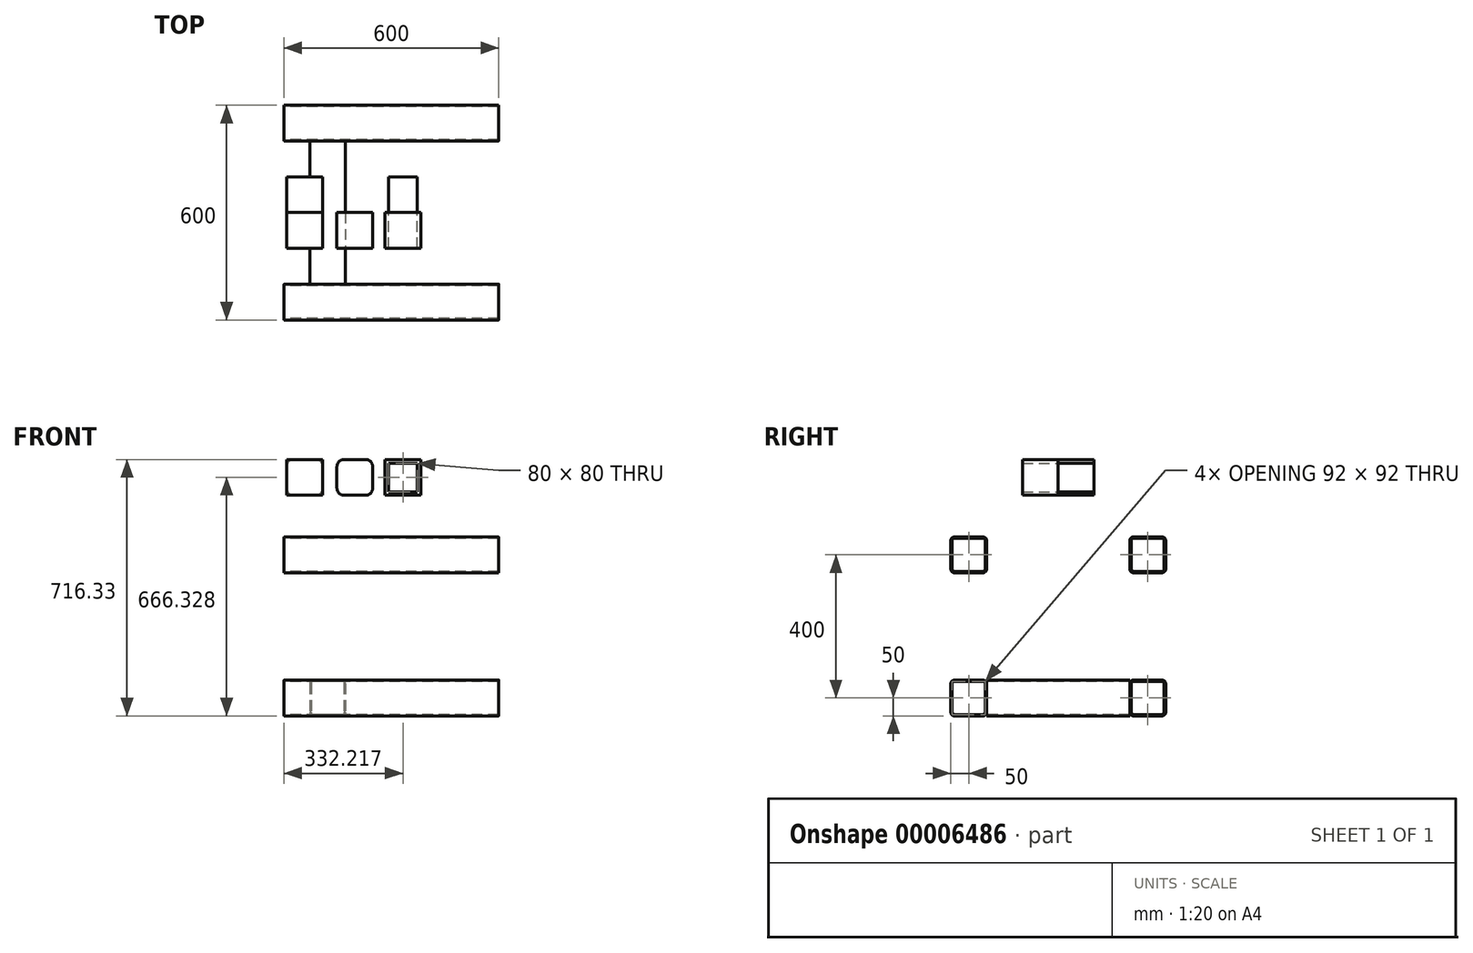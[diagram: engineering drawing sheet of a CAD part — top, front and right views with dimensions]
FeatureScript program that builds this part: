
annotation { "Feature Type Name" : "Feature", "Feature Type Description" : "" }
export const myFeature = defineFeature(function(context is Context, id is Id, definition is map)
    precondition{}
    {
        {
            var Q0;
            Q0=qCreatedBy(makeId("Right.planeOp"),FACE);
            var sketch = newSketch(context, id + "F0", { "sketchPlane" : qUnion([Q0])});
            skLineSegment(sketch, "E0.rect.bottom", {"start": v(-210, 0) * mm, "end": v(-290, 0) * mm});
            skLineSegment(sketch, "E0.rect.top", {"start": v(-210, -100) * mm, "end": v(-290, -100) * mm});
            skLineSegment(sketch, "E0.rect.left", {"start": v(-200, -10) * mm, "end": v(-200, -90) * mm});
            skLineSegment(sketch, "E0.rect.right", {"start": v(-300, -10) * mm, "end": v(-300, -90) * mm});
            skPoint(sketch, "E0.rect.middle", {"position": v(-250, -50) * mm});
            skPoint(sketch, "E1.visualSharp", {"position": v(-300, 0) * mm});
            skArc(sketch, "E1.filletArc", {"start": v(-290, 0) * mm, "mid": v(-297.07, -2.93) * mm, "end": v(-300, -10) * mm});
            skPoint(sketch, "E2.visualSharp", {"position": v(-200, 0) * mm});
            skArc(sketch, "E2.filletArc", {"start": v(-200, -10) * mm, "mid": v(-202.93, -2.93) * mm, "end": v(-210, 0) * mm});
            skPoint(sketch, "E3.visualSharp", {"position": v(-200, -100) * mm});
            skArc(sketch, "E3.filletArc", {"start": v(-210, -100) * mm, "mid": v(-202.93, -97.07) * mm, "end": v(-200, -90) * mm});
            skPoint(sketch, "E4.visualSharp", {"position": v(-300, -100) * mm});
            skArc(sketch, "E4.filletArc", {"start": v(-300, -90) * mm, "mid": v(-297.07, -97.07) * mm, "end": v(-290, -100) * mm});
            skArc(sketch, "E5.0", {"start": v(-204, -10) * mm, "mid": v(-205.76, -5.76) * mm, "end": v(-210, -4) * mm});
            skLineSegment(sketch, "E5.1", {"start": v(-204, -10) * mm, "end": v(-204, -90) * mm});
            skArc(sketch, "E5.2", {"start": v(-210, -96) * mm, "mid": v(-205.76, -94.24) * mm, "end": v(-204, -90) * mm});
            skLineSegment(sketch, "E5.3", {"start": v(-210, -96) * mm, "end": v(-290, -96) * mm});
            skArc(sketch, "E5.4", {"start": v(-296, -90) * mm, "mid": v(-294.24, -94.24) * mm, "end": v(-290, -96) * mm});
            skLineSegment(sketch, "E5.5", {"start": v(-210, -4) * mm, "end": v(-290, -4) * mm});
            skLineSegment(sketch, "E5.6", {"start": v(-296, -10) * mm, "end": v(-296, -90) * mm});
            skArc(sketch, "E5.7", {"start": v(-290, -4) * mm, "mid": v(-294.24, -5.76) * mm, "end": v(-296, -10) * mm});
            skLineSegment(sketch, "E6.0.1.0", {"start": v(-200, -410) * mm, "end": v(-200, -490) * mm});
            skPoint(sketch, "E6.0.1.1", {"position": v(-300, -400) * mm});
            skLineSegment(sketch, "E6.0.1.2", {"start": v(-210, -500) * mm, "end": v(-290, -500) * mm});
            skArc(sketch, "E6.0.1.3", {"start": v(-290, -400) * mm, "mid": v(-297.07, -402.93) * mm, "end": v(-300, -410) * mm});
            skPoint(sketch, "E6.0.1.4", {"position": v(-200, -500) * mm});
            skLineSegment(sketch, "E6.0.1.5", {"start": v(-210, -400) * mm, "end": v(-290, -400) * mm});
            skPoint(sketch, "E6.0.1.6", {"position": v(-300, -500) * mm});
            skLineSegment(sketch, "E6.0.1.7", {"start": v(-210, -496) * mm, "end": v(-290, -496) * mm});
            skLineSegment(sketch, "E6.0.1.8", {"start": v(-296, -410) * mm, "end": v(-296, -490) * mm});
            skPoint(sketch, "E6.0.1.9", {"position": v(-200, -400) * mm});
            skLineSegment(sketch, "E6.0.1.10", {"start": v(-204, -410) * mm, "end": v(-204, -490) * mm});
            skArc(sketch, "E6.0.1.11", {"start": v(-300, -490) * mm, "mid": v(-297.07, -497.07) * mm, "end": v(-290, -500) * mm});
            skArc(sketch, "E6.0.1.12", {"start": v(-204, -410) * mm, "mid": v(-205.76, -405.76) * mm, "end": v(-210, -404) * mm});
            skArc(sketch, "E6.0.1.13", {"start": v(-210, -500) * mm, "mid": v(-202.93, -497.07) * mm, "end": v(-200, -490) * mm});
            skLineSegment(sketch, "E6.0.1.14", {"start": v(-210, -404) * mm, "end": v(-290, -404) * mm});
            skLineSegment(sketch, "E6.0.1.15", {"start": v(-300, -410) * mm, "end": v(-300, -490) * mm});
            skArc(sketch, "E6.0.1.16", {"start": v(-296, -490) * mm, "mid": v(-294.24, -494.24) * mm, "end": v(-290, -496) * mm});
            skArc(sketch, "E6.0.1.17", {"start": v(-290, -404) * mm, "mid": v(-294.24, -405.76) * mm, "end": v(-296, -410) * mm});
            skArc(sketch, "E6.0.1.18", {"start": v(-210, -496) * mm, "mid": v(-205.76, -494.24) * mm, "end": v(-204, -490) * mm});
            skArc(sketch, "E6.0.1.19", {"start": v(-200, -410) * mm, "mid": v(-202.93, -402.93) * mm, "end": v(-210, -400) * mm});
            skPoint(sketch, "E6.0.1.20", {"position": v(-250, -450) * mm});
            skLineSegment(sketch, "E6.1.0.0", {"start": v(300, -10) * mm, "end": v(300, -90) * mm});
            skPoint(sketch, "E6.1.0.1", {"position": v(200, 0) * mm});
            skLineSegment(sketch, "E6.1.0.2", {"start": v(290, -100) * mm, "end": v(210, -100) * mm});
            skArc(sketch, "E6.1.0.3", {"start": v(210, 0) * mm, "mid": v(202.93, -2.93) * mm, "end": v(200, -10) * mm});
            skPoint(sketch, "E6.1.0.4", {"position": v(300, -100) * mm});
            skLineSegment(sketch, "E6.1.0.5", {"start": v(290, 0) * mm, "end": v(210, 0) * mm});
            skPoint(sketch, "E6.1.0.6", {"position": v(200, -100) * mm});
            skLineSegment(sketch, "E6.1.0.7", {"start": v(290, -96) * mm, "end": v(210, -96) * mm});
            skLineSegment(sketch, "E6.1.0.8", {"start": v(204, -10) * mm, "end": v(204, -90) * mm});
            skPoint(sketch, "E6.1.0.9", {"position": v(300, 0) * mm});
            skLineSegment(sketch, "E6.1.0.10", {"start": v(296, -10) * mm, "end": v(296, -90) * mm});
            skArc(sketch, "E6.1.0.11", {"start": v(200, -90) * mm, "mid": v(202.93, -97.07) * mm, "end": v(210, -100) * mm});
            skArc(sketch, "E6.1.0.12", {"start": v(296, -10) * mm, "mid": v(294.24, -5.76) * mm, "end": v(290, -4) * mm});
            skArc(sketch, "E6.1.0.13", {"start": v(290, -100) * mm, "mid": v(297.07, -97.07) * mm, "end": v(300, -90) * mm});
            skLineSegment(sketch, "E6.1.0.14", {"start": v(290, -4) * mm, "end": v(210, -4) * mm});
            skLineSegment(sketch, "E6.1.0.15", {"start": v(200, -10) * mm, "end": v(200, -90) * mm});
            skArc(sketch, "E6.1.0.16", {"start": v(204, -90) * mm, "mid": v(205.76, -94.24) * mm, "end": v(210, -96) * mm});
            skArc(sketch, "E6.1.0.17", {"start": v(210, -4) * mm, "mid": v(205.76, -5.76) * mm, "end": v(204, -10) * mm});
            skArc(sketch, "E6.1.0.18", {"start": v(290, -96) * mm, "mid": v(294.24, -94.24) * mm, "end": v(296, -90) * mm});
            skArc(sketch, "E6.1.0.19", {"start": v(300, -10) * mm, "mid": v(297.07, -2.93) * mm, "end": v(290, 0) * mm});
            skPoint(sketch, "E6.1.0.20", {"position": v(250, -50) * mm});
            skLineSegment(sketch, "E6.1.1.0", {"start": v(300, -410) * mm, "end": v(300, -490) * mm});
            skPoint(sketch, "E6.1.1.1", {"position": v(200, -400) * mm});
            skLineSegment(sketch, "E6.1.1.2", {"start": v(290, -500) * mm, "end": v(210, -500) * mm});
            skArc(sketch, "E6.1.1.3", {"start": v(210, -400) * mm, "mid": v(202.93, -402.93) * mm, "end": v(200, -410) * mm});
            skPoint(sketch, "E6.1.1.4", {"position": v(300, -500) * mm});
            skLineSegment(sketch, "E6.1.1.5", {"start": v(290, -400) * mm, "end": v(210, -400) * mm});
            skPoint(sketch, "E6.1.1.6", {"position": v(200, -500) * mm});
            skLineSegment(sketch, "E6.1.1.7", {"start": v(290, -496) * mm, "end": v(210, -496) * mm});
            skLineSegment(sketch, "E6.1.1.8", {"start": v(204, -410) * mm, "end": v(204, -490) * mm});
            skPoint(sketch, "E6.1.1.9", {"position": v(300, -400) * mm});
            skLineSegment(sketch, "E6.1.1.10", {"start": v(296, -410) * mm, "end": v(296, -490) * mm});
            skArc(sketch, "E6.1.1.11", {"start": v(200, -490) * mm, "mid": v(202.93, -497.07) * mm, "end": v(210, -500) * mm});
            skArc(sketch, "E6.1.1.12", {"start": v(296, -410) * mm, "mid": v(294.24, -405.76) * mm, "end": v(290, -404) * mm});
            skArc(sketch, "E6.1.1.13", {"start": v(290, -500) * mm, "mid": v(297.07, -497.07) * mm, "end": v(300, -490) * mm});
            skLineSegment(sketch, "E6.1.1.14", {"start": v(290, -404) * mm, "end": v(210, -404) * mm});
            skLineSegment(sketch, "E6.1.1.15", {"start": v(200, -410) * mm, "end": v(200, -490) * mm});
            skArc(sketch, "E6.1.1.16", {"start": v(204, -490) * mm, "mid": v(205.76, -494.24) * mm, "end": v(210, -496) * mm});
            skArc(sketch, "E6.1.1.17", {"start": v(210, -404) * mm, "mid": v(205.76, -405.76) * mm, "end": v(204, -410) * mm});
            skArc(sketch, "E6.1.1.18", {"start": v(290, -496) * mm, "mid": v(294.24, -494.24) * mm, "end": v(296, -490) * mm});
            skArc(sketch, "E6.1.1.19", {"start": v(300, -410) * mm, "mid": v(297.07, -402.93) * mm, "end": v(290, -400) * mm});
            skPoint(sketch, "E6.1.1.20", {"position": v(250, -450) * mm});
            skLineSegment(sketch, "E6.direction1", {"start": v(-250, -50) * mm, "end": v(250, -50) * mm, "construction": true});
            skLineSegment(sketch, "E6.direction2", {"start": v(-250, -50) * mm, "end": v(-250, -450) * mm, "construction": true});
            skLineSegment(sketch, "E7", {"start": v(0, 0) * mm, "end": v(0, -50) * mm, "construction": true});
            skSolve(sketch);
        }
        {
            var Q0;
            Q0=makeQuery(id+"F0.imprint","IMPRINT",FACE,{"disambiguationData":[TD([[makeQuery(id+"F0.imprint","IMPRINT",EDGE,{"derivedFrom":sQuery(id+"F0.wireOp",EDGE,"E0.rect.bottom")}),1.0]])]});
            var Q1;
            Q1=makeQuery(id+"F0.imprint","IMPRINT",FACE,{"disambiguationData":[TD([[makeQuery(id+"F0.imprint","IMPRINT",EDGE,{"derivedFrom":sQuery(id+"F0.wireOp",EDGE,"E6.1.0.0")}),-1.0]])]});
            var Q2;
            Q2=makeQuery(id+"F0.imprint","IMPRINT",FACE,{"disambiguationData":[TD([[makeQuery(id+"F0.imprint","IMPRINT",EDGE,{"derivedFrom":sQuery(id+"F0.wireOp",EDGE,"E6.0.1.0")}),-1.0]])]});
            var Q3;
            Q3=makeQuery(id+"F0.imprint","IMPRINT",FACE,{"disambiguationData":[TD([[makeQuery(id+"F0.imprint","IMPRINT",EDGE,{"derivedFrom":sQuery(id+"F0.wireOp",EDGE,"E6.1.1.0")}),-1.0]])]});
            extrude(context, id + "F1", {"entities" : qUnion([Q0, Q1, Q2, Q3]), "endBound" : BoundingType.SYMMETRIC, "depth" : 600 * mm});
        }
        {
            var Q0;
            Q0=qCreatedBy(makeId("Front.planeOp"),FACE);
            var sketch = newSketch(context, id + "F2", { "sketchPlane" : qUnion([Q0])});
            skLineSegment(sketch, "E8.rect.bottom", {"start": v(-127.9, -400) * mm, "end": v(-227.9, -400) * mm});
            skLineSegment(sketch, "E8.rect.top", {"start": v(-127.9, -500) * mm, "end": v(-227.9, -500) * mm});
            skLineSegment(sketch, "E8.rect.left", {"start": v(-127.9, -400) * mm, "end": v(-127.9, -500) * mm});
            skLineSegment(sketch, "E8.rect.right", {"start": v(-227.9, -400) * mm, "end": v(-227.9, -500) * mm});
            skPoint(sketch, "E8.rect.middle", {"position": v(-177.9, -450) * mm});
            skLineSegment(sketch, "E9.0", {"start": v(300, -500) * mm, "end": v(-300, -500) * mm});
            skLineSegment(sketch, "E10.0", {"start": v(300, -400) * mm, "end": v(-300, -400) * mm});
            skLineSegment(sketch, "E11.0", {"start": v(-223.9, -404) * mm, "end": v(-223.9, -496) * mm});
            skLineSegment(sketch, "E11.1", {"start": v(-131.9, -404) * mm, "end": v(-223.9, -404) * mm});
            skLineSegment(sketch, "E11.2", {"start": v(-131.9, -404) * mm, "end": v(-131.9, -496) * mm});
            skLineSegment(sketch, "E11.3", {"start": v(-131.9, -496) * mm, "end": v(-223.9, -496) * mm});
            skSolve(sketch);
        }
        {
            var Q0;
            Q0=makeQuery(id+"F2.imprint","IMPRINT",FACE,{"disambiguationData":[TD([[makeQuery(id+"F2.imprint","IMPRINT",EDGE,{"derivedFrom":sQuery(id+"F2.wireOp",EDGE,"E8.rect.bottom")}),1.0]])]});
            var Q1;
            Q1=makeQuery(id+"F1.opExtrude","SWEPT_BODY",BODY,{"disambiguationData":[OSD([sQuery(id+"F0.wireOp",EDGE,"E6.1.1.0"),sQuery(id+"F0.wireOp",EDGE,"E6.1.1.2"),sQuery(id+"F0.wireOp",EDGE,"E6.1.1.3"),sQuery(id+"F0.wireOp",EDGE,"E6.1.1.5"),sQuery(id+"F0.wireOp",EDGE,"E6.1.1.7"),sQuery(id+"F0.wireOp",EDGE,"E6.1.1.8"),sQuery(id+"F0.wireOp",EDGE,"E6.1.1.10"),sQuery(id+"F0.wireOp",EDGE,"E6.1.1.11"),sQuery(id+"F0.wireOp",EDGE,"E6.1.1.12"),sQuery(id+"F0.wireOp",EDGE,"E6.1.1.13"),sQuery(id+"F0.wireOp",EDGE,"E6.1.1.14"),sQuery(id+"F0.wireOp",EDGE,"E6.1.1.15"),sQuery(id+"F0.wireOp",EDGE,"E6.1.1.16"),sQuery(id+"F0.wireOp",EDGE,"E6.1.1.17"),sQuery(id+"F0.wireOp",EDGE,"E6.1.1.18"),sQuery(id+"F0.wireOp",EDGE,"E6.1.1.19")])]});
            extrude(context, id + "F3", {"entities" : qUnion([Q0]), "operationType" : NewBodyOperationType.ADD, "endBound" : BoundingType.SYMMETRIC, "oppositeDirection" : true, "endBoundEntity" : qUnion([Q1]), "depth" : 400 * mm});
        }
        {
            var Q0;
            Q0=makeQuery(id+"F3.opExtrude","SWEPT_EDGE",EDGE,{"disambiguationData":[OSD([sQuery(id+"F2.wireOp",EDGE,"E8.rect.bottom"),sQuery(id+"F2.wireOp",EDGE,"E8.rect.left")])]});
            fillet(context, id + "F4", {"entities" : qUnion([Q0]), "radius" : 10 * mm, "tangentPropagation" : true, "allowEdgeOverflow" : false});
        }
        {
            var Q0;
            Q0=qCreatedBy(makeId("Front.planeOp"),FACE);
            var sketch = newSketch(context, id + "F5", { "sketchPlane" : qUnion([Q0])});
            skLineSegment(sketch, "E12.rect.bottom", {"start": v(-191.9, 116.33) * mm, "end": v(-291.9, 116.33) * mm});
            skLineSegment(sketch, "E12.rect.top", {"start": v(-191.9, 216.33) * mm, "end": v(-291.9, 216.33) * mm});
            skLineSegment(sketch, "E12.rect.left", {"start": v(-191.9, 116.33) * mm, "end": v(-191.9, 216.33) * mm});
            skLineSegment(sketch, "E12.rect.right", {"start": v(-291.9, 116.33) * mm, "end": v(-291.9, 216.33) * mm});
            skPoint(sketch, "E12.rect.middle", {"position": v(-241.9, 166.33) * mm});
            skLineSegment(sketch, "E13.rect.bottom", {"start": v(82.22, 216.33) * mm, "end": v(-17.78, 216.33) * mm});
            skLineSegment(sketch, "E13.rect.top", {"start": v(82.22, 116.33) * mm, "end": v(-17.78, 116.33) * mm});
            skLineSegment(sketch, "E13.rect.left", {"start": v(82.22, 216.33) * mm, "end": v(82.22, 116.33) * mm});
            skLineSegment(sketch, "E13.rect.right", {"start": v(-17.78, 216.33) * mm, "end": v(-17.78, 116.33) * mm});
            skPoint(sketch, "E13.rect.middle", {"position": v(32.22, 166.33) * mm});
            skLineSegment(sketch, "E14.rect.bottom", {"start": v(-72.15, 216.33) * mm, "end": v(-132.15, 216.33) * mm});
            skLineSegment(sketch, "E14.rect.top", {"start": v(-72.15, 116.33) * mm, "end": v(-132.15, 116.33) * mm});
            skLineSegment(sketch, "E14.rect.left", {"start": v(-52.15, 196.33) * mm, "end": v(-52.15, 136.33) * mm});
            skLineSegment(sketch, "E14.rect.right", {"start": v(-152.15, 196.33) * mm, "end": v(-152.15, 136.33) * mm});
            skPoint(sketch, "E14.rect.middle", {"position": v(-102.15, 166.33) * mm});
            skPoint(sketch, "E15.visualSharp", {"position": v(-152.15, 216.33) * mm});
            skArc(sketch, "E15.filletArc", {"start": v(-132.15, 216.33) * mm, "mid": v(-146.29, 210.47) * mm, "end": v(-152.15, 196.33) * mm});
            skPoint(sketch, "E16.visualSharp", {"position": v(-52.15, 216.33) * mm});
            skArc(sketch, "E16.filletArc", {"start": v(-52.15, 196.33) * mm, "mid": v(-58, 210.47) * mm, "end": v(-72.15, 216.33) * mm});
            skPoint(sketch, "E17.visualSharp", {"position": v(-52.15, 116.33) * mm});
            skArc(sketch, "E17.filletArc", {"start": v(-72.15, 116.33) * mm, "mid": v(-58, 122.19) * mm, "end": v(-52.15, 136.33) * mm});
            skPoint(sketch, "E18.visualSharp", {"position": v(-152.15, 116.33) * mm});
            skArc(sketch, "E18.filletArc", {"start": v(-152.15, 136.33) * mm, "mid": v(-146.29, 122.19) * mm, "end": v(-132.15, 116.33) * mm});
            skLineSegment(sketch, "E19.0", {"start": v(72.22, 206.33) * mm, "end": v(-7.78, 206.33) * mm});
            skLineSegment(sketch, "E19.1", {"start": v(72.22, 206.33) * mm, "end": v(72.22, 126.33) * mm});
            skLineSegment(sketch, "E19.2", {"start": v(72.22, 126.33) * mm, "end": v(-7.78, 126.33) * mm});
            skLineSegment(sketch, "E19.3", {"start": v(-7.78, 206.33) * mm, "end": v(-7.78, 126.33) * mm});
            skSolve(sketch);
        }
        {
            var Q0;
            Q0=makeQuery(id+"F5.imprint","IMPRINT",FACE,{"disambiguationData":[TD([[makeQuery(id+"F5.imprint","IMPRINT",EDGE,{"derivedFrom":sQuery(id+"F5.wireOp",EDGE,"E12.rect.bottom")}),-1.0]])]});
            extrude(context, id + "F6", {"entities" : qUnion([Q0]), "depth" : 100 * mm});
        }
        {
            var Q0;
            Q0=makeQuery(id+"F5.imprint","IMPRINT",FACE,{"disambiguationData":[TD([[makeQuery(id+"F5.imprint","IMPRINT",EDGE,{"derivedFrom":sQuery(id+"F5.wireOp",EDGE,"E14.rect.bottom")}),1.0]])]});
            extrude(context, id + "F7", {"entities" : qUnion([Q0]), "depth" : 100 * mm});
        }
        {
            var Q0;
            Q0=makeQuery(id+"F5.imprint","IMPRINT",FACE,{"disambiguationData":[TD([[makeQuery(id+"F5.imprint","IMPRINT",EDGE,{"derivedFrom":sQuery(id+"F5.wireOp",EDGE,"E13.rect.bottom")}),1.0]])]});
            extrude(context, id + "F8", {"entities" : qUnion([Q0]), "depth" : 100 * mm});
        }
        {
            var Q0;
            Q0=makeQuery(id+"F5.imprint","IMPRINT",FACE,{"disambiguationData":[TD([[makeQuery(id+"F5.imprint","IMPRINT",EDGE,{"derivedFrom":sQuery(id+"F5.wireOp",EDGE,"E19.0")}),1.0]])]});
            extrude(context, id + "F9", {"entities" : qUnion([Q0]), "oppositeDirection" : true, "depth" : 100 * mm});
        }
        {
            var Q0;
            Q0=makeQuery(id+"F5.imprint","IMPRINT",FACE,{"disambiguationData":[TD([[makeQuery(id+"F5.imprint","IMPRINT",EDGE,{"derivedFrom":sQuery(id+"F5.wireOp",EDGE,"E12.rect.bottom")}),-1.0]])]});
            extrude(context, id + "F10", {"entities" : qUnion([Q0]), "oppositeDirection" : true, "depth" : 100 * mm});
        }
        {
            var Q0;
            Q0=makeQuery(id+"F10.opExtrude","SWEPT_EDGE",EDGE,{"disambiguationData":[OSD([sQuery(id+"F5.wireOp",EDGE,"E12.rect.top"),sQuery(id+"F5.wireOp",EDGE,"E12.rect.left")])]});
            var Q1;
            Q1=makeQuery(id+"F10.opExtrude","SWEPT_EDGE",EDGE,{"disambiguationData":[OSD([sQuery(id+"F5.wireOp",EDGE,"E12.rect.top"),sQuery(id+"F5.wireOp",EDGE,"E12.rect.right")])]});
            var Q2;
            Q2=makeQuery(id+"F10.opExtrude","SWEPT_EDGE",EDGE,{"disambiguationData":[OSD([sQuery(id+"F5.wireOp",EDGE,"E12.rect.bottom"),sQuery(id+"F5.wireOp",EDGE,"E12.rect.left")])]});
            var Q3;
            Q3=makeQuery(id+"F10.opExtrude","SWEPT_EDGE",EDGE,{"disambiguationData":[OSD([sQuery(id+"F5.wireOp",EDGE,"E12.rect.bottom"),sQuery(id+"F5.wireOp",EDGE,"E12.rect.right")])]});
            fillet(context, id + "F11", {"entities" : qUnion([Q0, Q1, Q2, Q3]), "radius" : 20 * mm, "tangentPropagation" : true, "allowEdgeOverflow" : false});
        }
    });
